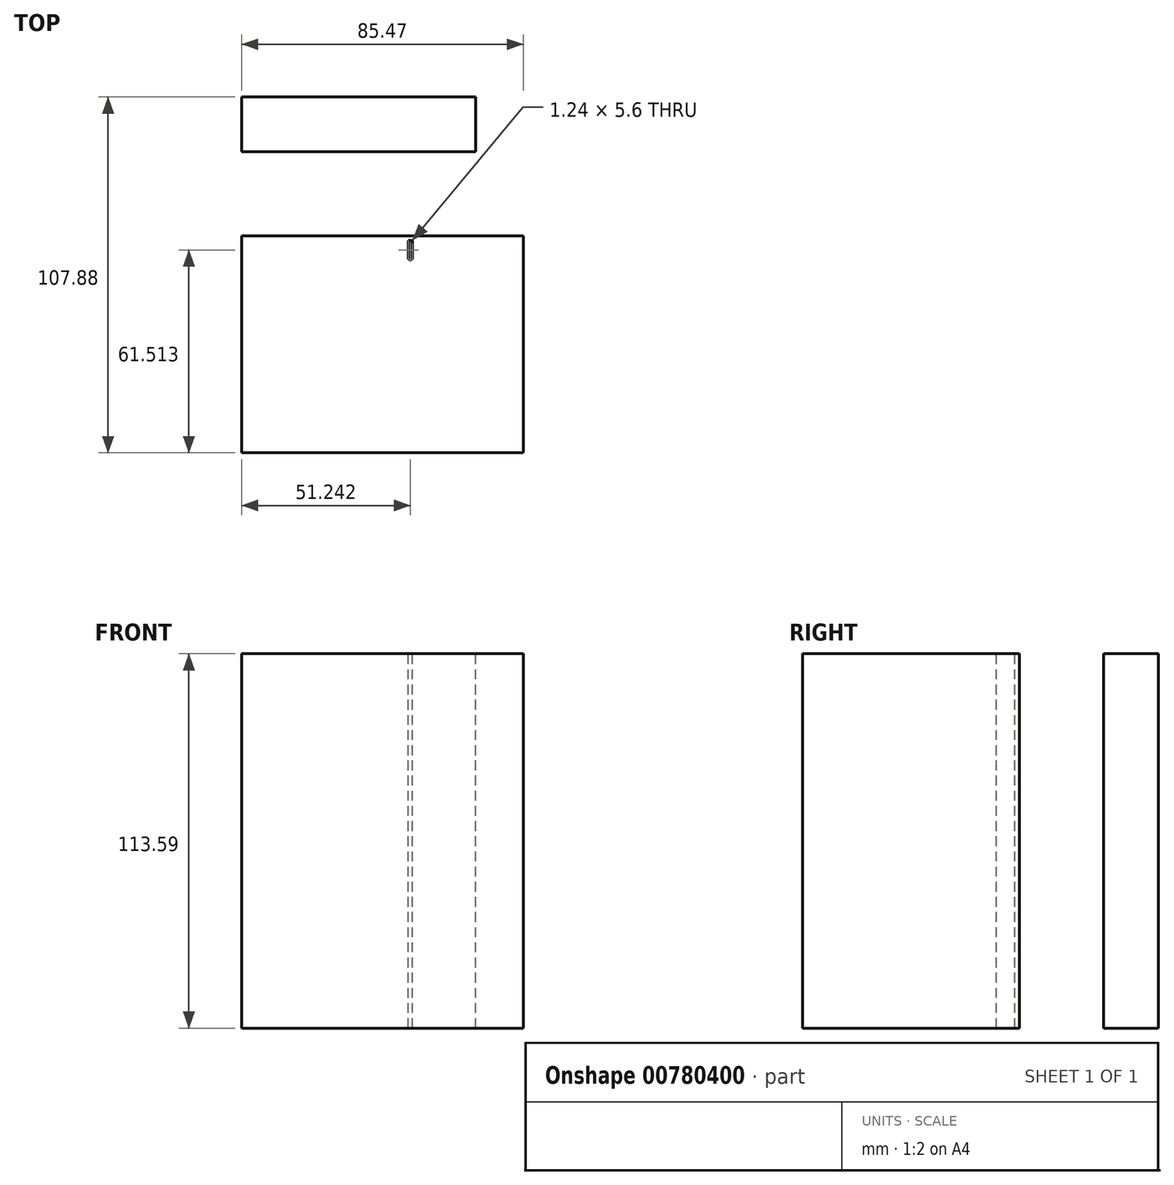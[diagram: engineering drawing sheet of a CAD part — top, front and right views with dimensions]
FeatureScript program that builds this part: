
annotation { "Feature Type Name" : "Feature", "Feature Type Description" : "" }
export const myFeature = defineFeature(function(context is Context, id is Id, definition is map)
    precondition{}
    {
        {
            var Q0;
            Q0=qCreatedBy(makeId("Top.planeOp"),FACE);
            var sketch = newSketch(context, id + "F0", { "sketchPlane" : qUnion([Q0])});
            skLineSegment(sketch, "E0.bottom", {"start": v(13.9, 18.46) * mm, "end": v(15.14, 18.46) * mm});
            skLineSegment(sketch, "E0.top", {"start": v(13.9, 12.86) * mm, "end": v(15.14, 12.86) * mm});
            skLineSegment(sketch, "E0.left", {"start": v(13.9, 18.46) * mm, "end": v(13.9, 12.86) * mm});
            skLineSegment(sketch, "E0.right", {"start": v(15.14, 18.46) * mm, "end": v(15.14, 12.86) * mm});
            skLineSegment(sketch, "E1.bottom", {"start": v(-37.34, 45.43) * mm, "end": v(-36.72, 45.43) * mm});
            skLineSegment(sketch, "E1.top", {"start": v(-37.34, 62.03) * mm, "end": v(-36.72, 62.03) * mm});
            skLineSegment(sketch, "E1.left", {"start": v(-37.34, 45.43) * mm, "end": v(-37.34, 62.03) * mm});
            skLineSegment(sketch, "E1.right", {"start": v(-36.72, 45.43) * mm, "end": v(-36.72, 62.03) * mm});
            skLineSegment(sketch, "E2.bottom", {"start": v(-36.72, 19.92) * mm, "end": v(48.75, 19.92) * mm});
            skLineSegment(sketch, "E2.top", {"start": v(-36.72, -45.85) * mm, "end": v(48.75, -45.85) * mm});
            skLineSegment(sketch, "E2.left", {"start": v(-36.72, 19.92) * mm, "end": v(-36.72, -45.85) * mm});
            skLineSegment(sketch, "E2.right", {"start": v(48.75, 19.92) * mm, "end": v(48.75, -45.85) * mm});
            skLineSegment(sketch, "E3.bottom", {"start": v(34.23, 62.03) * mm, "end": v(-37.34, 62.03) * mm});
            skLineSegment(sketch, "E3.top", {"start": v(34.23, 45.43) * mm, "end": v(-37.34, 45.43) * mm});
            skLineSegment(sketch, "E3.left", {"start": v(34.23, 62.03) * mm, "end": v(34.23, 45.43) * mm});
            skLineSegment(sketch, "E3.right", {"start": v(-37.34, 62.03) * mm, "end": v(-37.34, 45.43) * mm});
            skLineSegment(sketch, "E4.bottom", {"start": v(48.75, 19.92) * mm, "end": v(-36.72, 19.92) * mm});
            skLineSegment(sketch, "E4.top", {"start": v(48.75, 45.43) * mm, "end": v(-36.72, 45.43) * mm});
            skLineSegment(sketch, "E4.left", {"start": v(48.75, 19.92) * mm, "end": v(48.75, 45.43) * mm});
            skLineSegment(sketch, "E4.right", {"start": v(-36.72, 19.92) * mm, "end": v(-36.72, 45.43) * mm});
            skLineSegment(sketch, "E5.bottom", {"start": v(83.81, 0) * mm, "end": v(48.75, 0) * mm});
            skLineSegment(sketch, "E5.top", {"start": v(83.81, -45.85) * mm, "end": v(48.75, -45.85) * mm});
            skLineSegment(sketch, "E5.left", {"start": v(83.81, 0) * mm, "end": v(83.81, -45.85) * mm});
            skLineSegment(sketch, "E5.right", {"start": v(48.75, 0) * mm, "end": v(48.75, -45.85) * mm});
            skLineSegment(sketch, "E6.bottom", {"start": v(96.26, 10.37) * mm, "end": v(131.11, 10.37) * mm});
            skLineSegment(sketch, "E6.top", {"start": v(96.26, -98.33) * mm, "end": v(131.11, -98.33) * mm});
            skLineSegment(sketch, "E6.left", {"start": v(96.26, -98.33) * mm, "end": v(96.26, 10.37) * mm});
            skLineSegment(sketch, "E6.right", {"start": v(131.11, -98.33) * mm, "end": v(131.11, 10.37) * mm});
            skLineSegment(sketch, "E7.bottom", {"start": v(180.28, 37.96) * mm, "end": v(117.21, 37.96) * mm});
            skLineSegment(sketch, "E7.top", {"start": v(180.28, -98.33) * mm, "end": v(117.21, -98.33) * mm});
            skLineSegment(sketch, "E7.left", {"start": v(180.28, 37.96) * mm, "end": v(180.28, -98.33) * mm});
            skLineSegment(sketch, "E7.right", {"start": v(117.21, 37.96) * mm, "end": v(117.21, -98.33) * mm});
            skLineSegment(sketch, "E8.bottom", {"start": v(249.99, -98.33) * mm, "end": v(154.56, -98.33) * mm});
            skLineSegment(sketch, "E8.top", {"start": v(249.99, 93.56) * mm, "end": v(154.56, 93.56) * mm});
            skLineSegment(sketch, "E8.left", {"start": v(249.99, -98.33) * mm, "end": v(249.99, 93.56) * mm});
            skLineSegment(sketch, "E8.right", {"start": v(154.56, -98.33) * mm, "end": v(154.56, 93.56) * mm});
            skSolve(sketch);
        }
        {
            var Q0;
            Q0=makeQuery(id+"F0.imprint","IMPRINT",FACE,{"disambiguationData":[TD([[makeQuery(id+"F0.imprint","IMPRINT",EDGE,{"derivedFrom":sQuery(id+"F0.wireOp",EDGE,"E0.bottom")}),1.0]])]});
            var Q1;
            {var subQ0=sQuery(id+"F0.wireOp",EDGE,"E1.right");Q1=makeQuery(id+"F0.imprint","IMPRINT",FACE,{"disambiguationData":[TD([[makeQuery(id+"F0.imprint","IMPRINT",EDGE,{"derivedFrom":subQ0}),-1.0]])]});}
            extrude(context, id + "F1", {"entities" : qUnion([Q0, Q1]), "oppositeDirection" : true, "depth" : 113.6 * mm, "offsetDistance" : 25.4 * mm});
        }
    });
